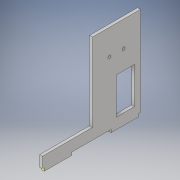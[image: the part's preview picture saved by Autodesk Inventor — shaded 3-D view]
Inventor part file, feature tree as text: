
AUTODESK INVENTOR PART (.ipt)
format: ipt  version: 2019 (Build 230136000, 136)  size: 140,800 bytes
history: native  units: in
note: dims shown in document units (in); Inventor stores cm internally (conversion verified against a paired STEP export)
features: sketch x5, extrude x4
ambient origin geometry x8: Origin, YZ Plane, XZ Plane, XY Plane, X Axis, Y Axis, Z Axis, Center Point
bodies: Solid1 (feature_tree)
feature tree (9):
  extrude  "Extrusion1"  Depth=0.125in
  extrude  "Extrusion2"  Depth=1.2in
  sketch  "Sketch3"  dims[d4=1.2in d5=0.075in]
  extrude  "Extrusion3"  Depth=0.075in
  extrude  "Extrusion4"  Depth=3.875in
  sketch  "Sketch1"  dims[d0=4.25in d1=0.125in]
  sketch  "Sketch2"  dims[d2=0.125in d3=1.2in]
  sketch  "Sketch4"  dims[d6=0.075in d7=3.875in]
  sketch  "Sketch5"  dims[d8=0.125in d9=0.0in d10=1.585in d11=0.8in d12=0.35in d14=0.25in d15=0.125in d16=0.0in d17=0.125in d18=0.0in d19=0.13in d20=0.13in d21=0.615in d22=0.7325in d23=0.0in d24=0.125in d25=0.0in]
